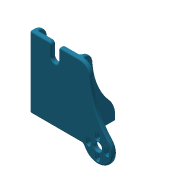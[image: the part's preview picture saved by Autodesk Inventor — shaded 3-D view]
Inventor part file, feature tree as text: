
AUTODESK INVENTOR PART (.ipt)
format: ipt  version: 2014 (Build 180170000, 170)  size: 872,448 bytes
history: native  units: mm
features: fillet x12, extrude x9, sketch x8, mirror x1
ambient origin geometry x8: Origin, YZ Plane, XZ Plane, XY Plane, X Axis, Y Axis, Z Axis, Center Point
bodies: Solid1 (feature_tree)
feature tree (30):
  extrude  "Extrusion1"  Depth=41.0mm
  extrude  "Extrusion2"  Depth=45.0mm
  extrude  "Extrusion3"  Depth=7.0mm TaperAngle=0.0deg
  mirror  "Mirror1"
  sketch  "Sketch4"  dims[d4=4.8mm d5=7.0mm d6=0.0mm]
  extrude  "Extrusion5"  Depth=10.0mm TaperAngle=0.0deg
  extrude  "Extrusion6"  Depth=12.0mm
  extrude  "Extrusion7"  Depth=25.0mm
  extrude  "Extrusion8"  Depth=2.0mm TaperAngle=0.0deg
  extrude  "Extrusion9"  Depth=2.0mm
  extrude  "Extrusion10"  Depth=2.0mm
  fillet  "Fillet1"  Radius=3.5mm
  fillet  "Fillet2"  Radius=4.5mm
  fillet  "Fillet3"  Radius=2.5mm
  fillet  "Fillet5"  Radius=2.5mm
  fillet  "Fillet6"  Radius=6.0mm
  fillet  "Fillet7"  Radius=7.0mm
  fillet  "Fillet8"  Radius=6.0mm
  fillet  "Fillet9"  Radius=15.0mm
  fillet  "Fillet10"  Radius=15.0mm
  fillet  "Fillet11"  Radius=6.0mm
  fillet  "Fillet12"  Radius=6.0mm
  fillet  "Fillet13"  Radius=6.0mm
  sketch  "Sketch1"  dims[d0=26.0mm d1=41.0mm]
  sketch  "Sketch2"  dims[d2=70.0mm d3=45.0mm]
  sketch  "Sketch5"  dims[d7=10.0mm d10=6.0mm d11=0.0mm]
  sketch  "Sketch6"  dims[d12=6.0mm d13=0.0mm d14=12.0mm]
  sketch  "Sketch7"  dims[d15=15.0mm d17=25.0mm]
  sketch  "Sketch8"  dims[d20=10.75mm d21=2.0mm d22=0.0mm]
  sketch  "Sketch9"  dims[d23=6.0mm d24=13.0mm d25=13.0mm d26=3.5mm d27=4.5mm d28=2.5mm d29=2.5mm d30=6.0mm d31=0.0mm d32=7.0mm d33=0.0mm d34=6.0mm d35=15.0mm d36=15.0mm d37=6.0mm d38=6.0mm d39=6.0mm d40=10.0mm d41=6.0mm d42=2.0mm d43=0.0mm d44=5.75mm d45=2.5mm d46=0.0mm d47=4.0mm d48=2.0mm d49=2.0mm d51=2.0mm d52=2.0mm d53=2.0mm d54=2.0mm d55=1.0mm d56=2.0mm d57=0.75mm d58=30.0mm d59=45.0mm d60=15.0mm d61=6.0mm d62=0.0mm d63=2.0mm d64=2.0mm d65=82.5mm d66=100.0mm d67=60.0mm]
